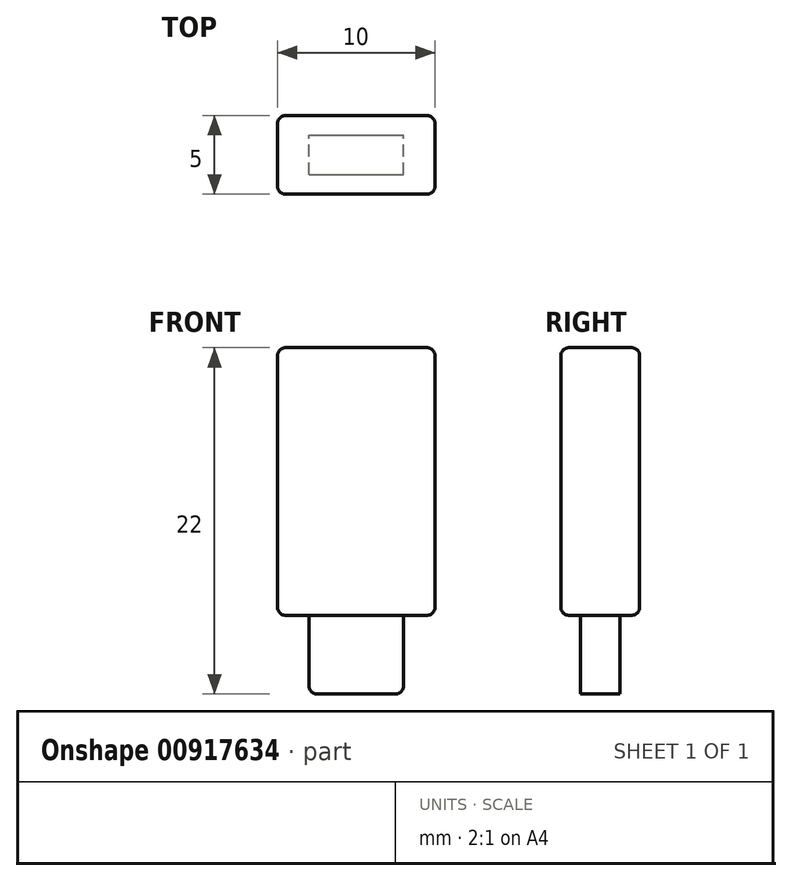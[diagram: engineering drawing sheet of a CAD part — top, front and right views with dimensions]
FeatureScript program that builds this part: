
annotation { "Feature Type Name" : "Feature", "Feature Type Description" : "" }
export const myFeature = defineFeature(function(context is Context, id is Id, definition is map)
    precondition{}
    {
        {
            var Q0;
            Q0=qCreatedBy(makeId("Top.planeOp"),FACE);
            var sketch = newSketch(context, id + "F0", { "sketchPlane" : qUnion([Q0])});
            skLineSegment(sketch, "E0.bottom", {"start": v(-6.28, 0.48) * mm, "end": v(3.72, 0.48) * mm});
            skLineSegment(sketch, "E0.top", {"start": v(-6.28, -4.52) * mm, "end": v(3.72, -4.52) * mm});
            skLineSegment(sketch, "E0.left", {"start": v(-6.28, 0.48) * mm, "end": v(-6.28, -4.52) * mm});
            skLineSegment(sketch, "E0.right", {"start": v(3.72, 0.48) * mm, "end": v(3.72, -4.52) * mm});
            skSolve(sketch);
        }
        {
            var Q0;
            Q0=makeQuery(id+"F0.imprint","IMPRINT",FACE,{"disambiguationData":[TD([[makeQuery(id+"F0.imprint","IMPRINT",EDGE,{"derivedFrom":sQuery(id+"F0.wireOp",EDGE,"E0.bottom")}),-1.0]])]});
            extrude(context, id + "F1", {"entities" : qUnion([Q0]), "depth" : 17 * mm, "offsetDistance" : 25.4 * mm});
        }
        {
            var Q0;
            Q0=makeQuery(id+"F1.opExtrude","CAP_FACE",FACE,{"disambiguationData":[OSD([sQuery(id+"F0.wireOp",EDGE,"E0.bottom"),sQuery(id+"F0.wireOp",EDGE,"E0.top"),sQuery(id+"F0.wireOp",EDGE,"E0.left"),sQuery(id+"F0.wireOp",EDGE,"E0.right")])],"isStart":true});
            var sketch = newSketch(context, id + "F2", { "sketchPlane" : qUnion([Q0])});
            skLineSegment(sketch, "E1.bottom", {"start": v(-4.28, 3.27) * mm, "end": v(1.72, 3.27) * mm});
            skLineSegment(sketch, "E1.top", {"start": v(-4.28, 0.77) * mm, "end": v(1.72, 0.77) * mm});
            skLineSegment(sketch, "E1.left", {"start": v(-4.28, 3.27) * mm, "end": v(-4.28, 0.77) * mm});
            skLineSegment(sketch, "E1.right", {"start": v(1.72, 3.27) * mm, "end": v(1.72, 0.77) * mm});
            skPoint(sketch, "E1.middle", {"position": v(-1.28, 2.02) * mm});
            skSolve(sketch);
        }
        {
            var Q0;
            Q0=makeQuery(id+"F2.imprint","IMPRINT",FACE,{"disambiguationData":[TD([[makeQuery(id+"F2.imprint","IMPRINT",EDGE,{"derivedFrom":sQuery(id+"F2.wireOp",EDGE,"E1.bottom")}),-1.0]])]});
            extrude(context, id + "F3", {"entities" : qUnion([Q0]), "operationType" : NewBodyOperationType.ADD, "depth" : 5 * mm, "offsetDistance" : 25.4 * mm});
        }
        {
            var Q0;
            Q0=makeQuery(id+"F3.opExtrude","CAP_EDGE",EDGE,{"disambiguationData":[OSD([sQuery(id+"F2.wireOp",EDGE,"E1.top")])],"isStart":true});
            var Q1;
            Q1=makeQuery(id+"F3.opExtrude","CAP_EDGE",EDGE,{"disambiguationData":[OSD([sQuery(id+"F2.wireOp",EDGE,"E1.right")])],"isStart":true});
            var Q2;
            Q2=makeQuery(id+"F3.opExtrude","CAP_EDGE",EDGE,{"disambiguationData":[OSD([sQuery(id+"F2.wireOp",EDGE,"E1.left")])],"isStart":true});
            var Q3;
            Q3=makeQuery(id+"F3.opExtrude","CAP_EDGE",EDGE,{"disambiguationData":[OSD([sQuery(id+"F2.wireOp",EDGE,"E1.bottom")])],"isStart":true});
            var Q4;
            Q4=makeQuery(id+"F3.opExtrude","CAP_EDGE",EDGE,{"disambiguationData":[OSD([sQuery(id+"F2.wireOp",EDGE,"E1.left")])],"isStart":false});
            var Q5;
            Q5=makeQuery(id+"F3.opExtrude","CAP_EDGE",EDGE,{"disambiguationData":[OSD([sQuery(id+"F2.wireOp",EDGE,"E1.right")])],"isStart":false});
            var Q6;
            Q6=makeQuery(id+"F1.opExtrude","CAP_EDGE",EDGE,{"disambiguationData":[OSD([sQuery(id+"F0.wireOp",EDGE,"E0.right")])],"isStart":true});
            var Q7;
            Q7=makeQuery(id+"F1.opExtrude","CAP_EDGE",EDGE,{"disambiguationData":[OSD([sQuery(id+"F0.wireOp",EDGE,"E0.bottom")])],"isStart":true});
            var Q8;
            Q8=makeQuery(id+"F1.opExtrude","SWEPT_EDGE",EDGE,{"disambiguationData":[OSD([sQuery(id+"F0.wireOp",EDGE,"E0.bottom"),sQuery(id+"F0.wireOp",EDGE,"E0.right")])]});
            var Q9;
            Q9=makeQuery(id+"F1.opExtrude","SWEPT_EDGE",EDGE,{"disambiguationData":[OSD([sQuery(id+"F0.wireOp",EDGE,"E0.bottom"),sQuery(id+"F0.wireOp",EDGE,"E0.left")])]});
            var Q10;
            Q10=makeQuery(id+"F1.opExtrude","CAP_EDGE",EDGE,{"disambiguationData":[OSD([sQuery(id+"F0.wireOp",EDGE,"E0.left")])],"isStart":true});
            var Q11;
            Q11=makeQuery(id+"F1.opExtrude","SWEPT_FACE",FACE,{"disambiguationData":[OSD([sQuery(id+"F0.wireOp",EDGE,"E0.top")])]});
            var Q12;
            Q12=makeQuery(id+"F1.opExtrude","CAP_FACE",FACE,{"disambiguationData":[OSD([sQuery(id+"F0.wireOp",EDGE,"E0.bottom"),sQuery(id+"F0.wireOp",EDGE,"E0.top"),sQuery(id+"F0.wireOp",EDGE,"E0.left"),sQuery(id+"F0.wireOp",EDGE,"E0.right")])],"isStart":false});
            fillet(context, id + "F4", {"entities" : qUnion([Q0, Q1, Q2, Q3, Q4, Q5, Q6, Q7, Q8, Q9, Q10, Q11, Q12]), "radius" : 0.5 * mm, "tangentPropagation" : true, "allowEdgeOverflow" : false});
        }
    });
